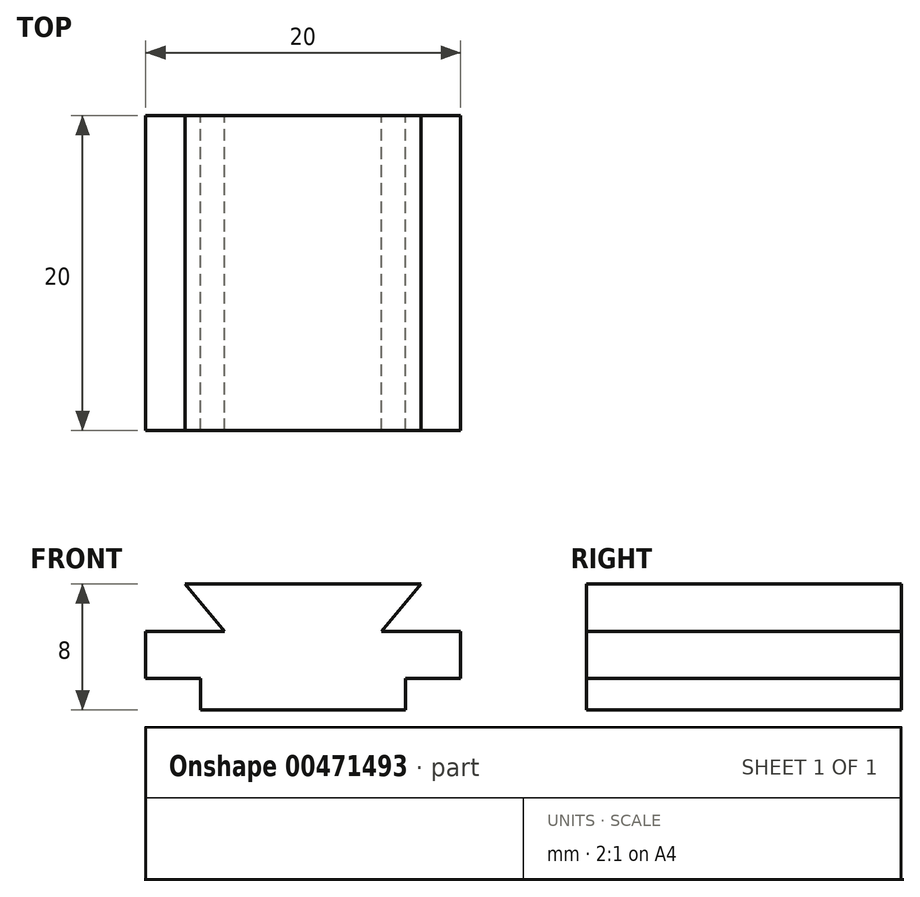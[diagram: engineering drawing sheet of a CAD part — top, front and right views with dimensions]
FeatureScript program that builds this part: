
annotation { "Feature Type Name" : "Feature", "Feature Type Description" : "" }
export const myFeature = defineFeature(function(context is Context, id is Id, definition is map)
    precondition{}
    {
        {
            var Q0;
            Q0=qCreatedBy(makeId("Front.planeOp"),FACE);
            var sketch = newSketch(context, id + "F0", { "sketchPlane" : qUnion([Q0])});
            skLineSegment(sketch, "E0", {"start": v(0, 18.9) * mm, "end": v(0, -22.99) * mm, "construction": true});
            skLineSegment(sketch, "E1", {"start": v(0, -8) * mm, "end": v(-6.5, -8) * mm});
            skLineSegment(sketch, "E2", {"start": v(-6.5, -8) * mm, "end": v(-6.5, -6) * mm});
            skLineSegment(sketch, "E3", {"start": v(-6.5, -6) * mm, "end": v(-10, -6) * mm});
            skLineSegment(sketch, "E4", {"start": v(-10, -6) * mm, "end": v(-10, -3) * mm});
            skLineSegment(sketch, "E5", {"start": v(-10, -3) * mm, "end": v(-4.98, -3) * mm});
            skLineSegment(sketch, "E6", {"start": v(-4.98, -3) * mm, "end": v(-7.5, 0) * mm});
            skLineSegment(sketch, "E7", {"start": v(-7.5, 0) * mm, "end": v(0, 0) * mm});
            skLineSegment(sketch, "E8.MirrorCS", {"start": v(0, -8) * mm, "end": v(6.5, -8) * mm});
            skLineSegment(sketch, "E9.MirrorCS", {"start": v(10, -6) * mm, "end": v(10, -3) * mm});
            skLineSegment(sketch, "E10.MirrorCS", {"start": v(10, -3) * mm, "end": v(4.98, -3) * mm});
            skLineSegment(sketch, "E11.MirrorCS", {"start": v(6.5, -6) * mm, "end": v(10, -6) * mm});
            skLineSegment(sketch, "E12.MirrorCS", {"start": v(7.5, 0) * mm, "end": v(0, 0) * mm});
            skLineSegment(sketch, "E13.MirrorCS", {"start": v(4.98, -3) * mm, "end": v(7.5, 0) * mm});
            skLineSegment(sketch, "E14.MirrorCS", {"start": v(6.5, -8) * mm, "end": v(6.5, -6) * mm});
            skSolve(sketch);
        }
        {
            var Q0;
            Q0=makeQuery(id+"F0.imprint","IMPRINT",FACE,{"disambiguationData":[TD([[makeQuery(id+"F0.imprint","IMPRINT",EDGE,{"derivedFrom":sQuery(id+"F0.wireOp",EDGE,"E1")}),-1.0]])]});
            extrude(context, id + "F1", {"entities" : qUnion([Q0]), "depth" : 20 * mm});
        }
    });
